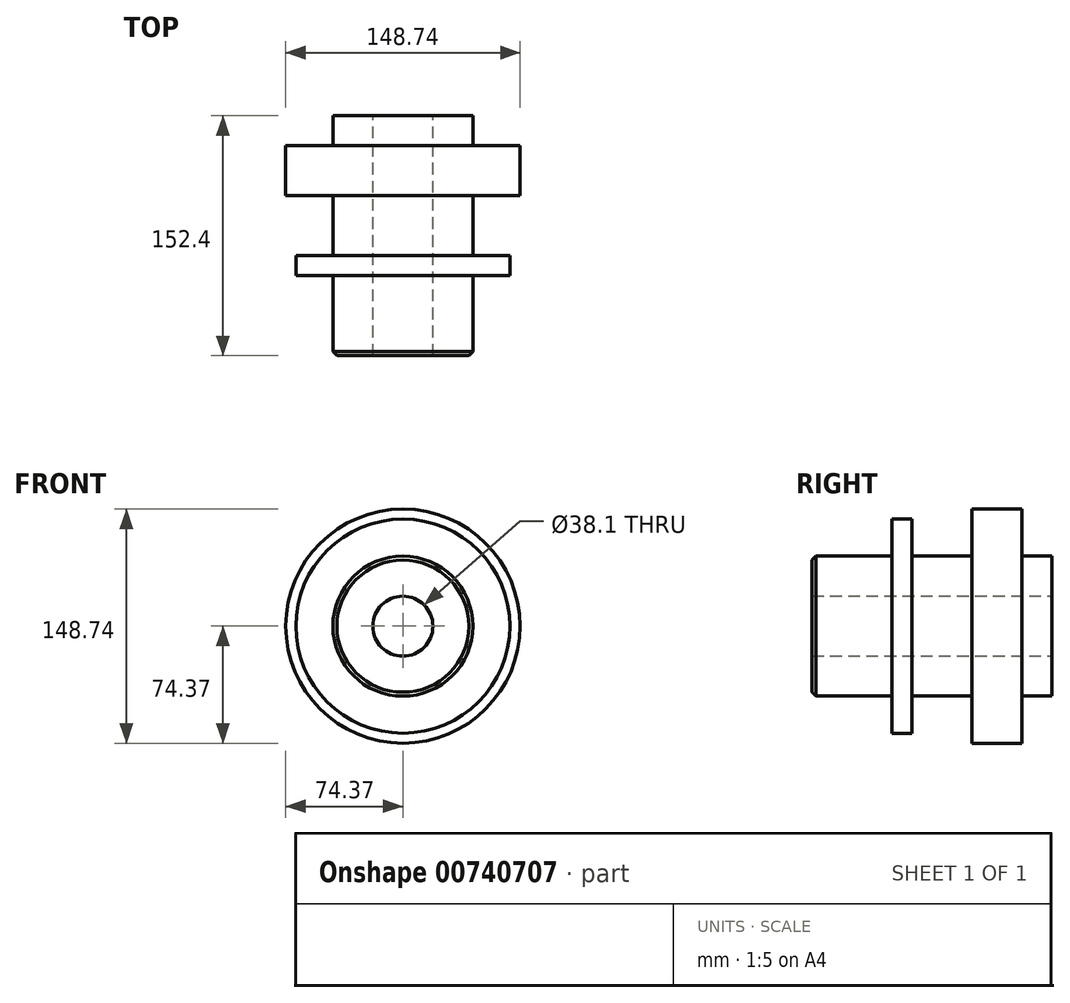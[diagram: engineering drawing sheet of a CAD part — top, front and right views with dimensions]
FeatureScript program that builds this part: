
annotation { "Feature Type Name" : "Feature", "Feature Type Description" : "" }
export const myFeature = defineFeature(function(context is Context, id is Id, definition is map)
    precondition{}
    {
        {
            var Q0;
            Q0=qCreatedBy(makeId("Right.planeOp"),FACE);
            var sketch = newSketch(context, id + "F0", { "sketchPlane" : qUnion([Q0])});
            skLineSegment(sketch, "E0", {"start": v(0, 0) * mm, "end": v(101, 0) * mm, "construction": true});
            skLineSegment(sketch, "E1.bottom", {"start": v(0, 19.05) * mm, "end": v(50.8, 19.05) * mm});
            skLineSegment(sketch, "E1.top", {"start": v(0, 44.45) * mm, "end": v(50.8, 44.45) * mm});
            skLineSegment(sketch, "E1.left", {"start": v(0, 19.05) * mm, "end": v(0, 44.45) * mm});
            skLineSegment(sketch, "E1.right", {"start": v(50.8, 19.05) * mm, "end": v(50.8, 44.45) * mm});
            skLineSegment(sketch, "E2.bottom", {"start": v(0, 19.05) * mm, "end": v(31.75, 19.05) * mm});
            skLineSegment(sketch, "E2.top", {"start": v(0, 74.37) * mm, "end": v(31.75, 74.37) * mm});
            skLineSegment(sketch, "E2.left", {"start": v(0, 19.05) * mm, "end": v(0, 74.37) * mm});
            skLineSegment(sketch, "E2.right", {"start": v(31.75, 19.05) * mm, "end": v(31.75, 74.37) * mm});
            skLineSegment(sketch, "E3.bottom", {"start": v(0, 44.45) * mm, "end": v(-50.8, 44.45) * mm});
            skLineSegment(sketch, "E3.top", {"start": v(0, 19.05) * mm, "end": v(-50.8, 19.05) * mm});
            skLineSegment(sketch, "E3.left", {"start": v(0, 44.45) * mm, "end": v(0, 19.05) * mm});
            skLineSegment(sketch, "E4.bottom", {"start": v(-50.8, 19.05) * mm, "end": v(-38.1, 19.05) * mm});
            skLineSegment(sketch, "E4.top", {"start": v(-50.8, 67.97) * mm, "end": v(-38.1, 67.97) * mm});
            skLineSegment(sketch, "E4.left", {"start": v(-50.8, 19.05) * mm, "end": v(-50.8, 67.97) * mm});
            skLineSegment(sketch, "E4.right", {"start": v(-38.1, 19.05) * mm, "end": v(-38.1, 67.97) * mm});
            skLineSegment(sketch, "E5.bottom", {"start": v(-50.8, 44.45) * mm, "end": v(-101.6, 44.45) * mm});
            skLineSegment(sketch, "E5.top", {"start": v(-50.8, 19.05) * mm, "end": v(-101.6, 19.05) * mm});
            skLineSegment(sketch, "E5.left", {"start": v(-50.8, 44.45) * mm, "end": v(-50.8, 19.05) * mm});
            skLineSegment(sketch, "E5.right", {"start": v(-101.6, 44.45) * mm, "end": v(-101.6, 19.05) * mm});
            skLineSegment(sketch, "E6.MirrorCS", {"start": v(0, -19.05) * mm, "end": v(0, -44.45) * mm});
            skLineSegment(sketch, "E7.MirrorCS", {"start": v(-50.8, -44.45) * mm, "end": v(-101.6, -44.45) * mm});
            skLineSegment(sketch, "E8.MirrorCS", {"start": v(-50.8, -44.45) * mm, "end": v(-50.8, -19.05) * mm});
            skLineSegment(sketch, "E9.MirrorCS", {"start": v(-50.8, -19.05) * mm, "end": v(-38.1, -19.05) * mm});
            skLineSegment(sketch, "E10.MirrorCS", {"start": v(-101.6, -44.45) * mm, "end": v(-101.6, -19.05) * mm});
            skLineSegment(sketch, "E11.MirrorCS", {"start": v(-50.8, -19.05) * mm, "end": v(-101.6, -19.05) * mm});
            skLineSegment(sketch, "E12.MirrorCS", {"start": v(-50.8, -67.97) * mm, "end": v(-38.1, -67.97) * mm});
            skLineSegment(sketch, "E13.MirrorCS", {"start": v(0, -44.45) * mm, "end": v(0, -19.05) * mm});
            skLineSegment(sketch, "E14.MirrorCS", {"start": v(0, -19.05) * mm, "end": v(-50.8, -19.05) * mm});
            skLineSegment(sketch, "E15.MirrorCS", {"start": v(0, -44.45) * mm, "end": v(-50.8, -44.45) * mm});
            skLineSegment(sketch, "E16.MirrorCS", {"start": v(0, -19.05) * mm, "end": v(50.8, -19.05) * mm});
            skLineSegment(sketch, "E17.MirrorCS", {"start": v(-50.8, -19.05) * mm, "end": v(-50.8, -67.97) * mm});
            skLineSegment(sketch, "E18.MirrorCS", {"start": v(0, -44.45) * mm, "end": v(50.8, -44.45) * mm});
            skLineSegment(sketch, "E19.MirrorCS", {"start": v(50.8, -19.05) * mm, "end": v(50.8, -44.45) * mm});
            skLineSegment(sketch, "E20.MirrorCS", {"start": v(31.75, -19.05) * mm, "end": v(31.75, -74.37) * mm});
            skLineSegment(sketch, "E21.MirrorCS", {"start": v(0, -19.05) * mm, "end": v(0, -74.37) * mm});
            skLineSegment(sketch, "E22.MirrorCS", {"start": v(0, -74.37) * mm, "end": v(31.75, -74.37) * mm});
            skLineSegment(sketch, "E23.MirrorCS", {"start": v(-38.1, -19.05) * mm, "end": v(-38.1, -67.97) * mm});
            skLineSegment(sketch, "E24.MirrorCS", {"start": v(0, -19.05) * mm, "end": v(31.75, -19.05) * mm});
            skLineSegment(sketch, "E25", {"start": v(0, 0) * mm, "end": v(-101.6, 0) * mm, "construction": true});
            skSolve(sketch);
        }
        {
            var Q0;
            {var subQ4=sQuery(id+"F0.wireOp",EDGE,"E4.bottom");Q0=makeQuery(id+"F0.imprint","IMPRINT",FACE,{"disambiguationData":[TD([[makeQuery(id+"F0.imprint","IMPRINT",EDGE,{"derivedFrom":subQ4}),1.0]])]});}
            var Q1;
            Q1=makeQuery(id+"F0.imprint","IMPRINT",FACE,{"disambiguationData":[TD([[makeQuery(id+"F0.imprint","IMPRINT",EDGE,{"derivedFrom":sQuery(id+"F0.wireOp",EDGE,"E5.bottom")}),1.0]])]});
            var Q2;
            {var subQ0=sQuery(id+"F0.wireOp",EDGE,"E1.bottom");Q2=makeQuery(id+"F0.imprint","IMPRINT",FACE,{"disambiguationData":[TD([[makeQuery(id+"F0.imprint","IMPRINT",EDGE,{"derivedFrom":subQ0}),1.0]])]});}
            var Q3;
            {var subQ4=sQuery(id+"F0.wireOp",EDGE,"E2.top");Q3=makeQuery(id+"F0.imprint","IMPRINT",FACE,{"disambiguationData":[TD([[makeQuery(id+"F0.imprint","IMPRINT",EDGE,{"derivedFrom":subQ4}),-1.0]])]});}
            var Q4;
            {var subQ4=sQuery(id+"F0.wireOp",EDGE,"E4.top");Q4=makeQuery(id+"F0.imprint","IMPRINT",FACE,{"disambiguationData":[TD([[makeQuery(id+"F0.imprint","IMPRINT",EDGE,{"derivedFrom":subQ4}),-1.0]])]});}
            var Q5;
            {var subQ4=sQuery(id+"F0.wireOp",EDGE,"E3.top");Q5=makeQuery(id+"F0.imprint","IMPRINT",FACE,{"disambiguationData":[TD([[makeQuery(id+"F0.imprint","IMPRINT",EDGE,{"derivedFrom":subQ4}),-1.0]])]});}
            var Q6;
            {var subQ4=sQuery(id+"F0.wireOp",EDGE,"E2.bottom");Q6=makeQuery(id+"F0.imprint","IMPRINT",FACE,{"disambiguationData":[TD([[makeQuery(id+"F0.imprint","IMPRINT",EDGE,{"derivedFrom":subQ4}),1.0]])]});}
            var Q7;
            Q7=sQuery(id+"F0.wireOp",EDGE,"E25");
            revolve(context, id + "F1", {"surfaceOperationType" : NewSurfaceOperationType.NEW, "entities" : qUnion([Q0, Q1, Q2, Q3, Q4, Q5, Q6]), "axis" : qUnion([Q7]), "revolveType" : RevolveType.FULL});
        }
        {
            var Q0;
            Q0=makeQuery(id+"F1.opRevolve","SWEPT_EDGE",EDGE,{"disambiguationData":[OSD([sQuery(id+"F0.wireOp",EDGE,"E5.bottom"),sQuery(id+"F0.wireOp",EDGE,"E5.right")])]});
            chamfer(context, id + "F2", {"entities" : qUnion([Q0]), "width" : 2.54 * mm, "tangentPropagation" : true});
        }
    });
